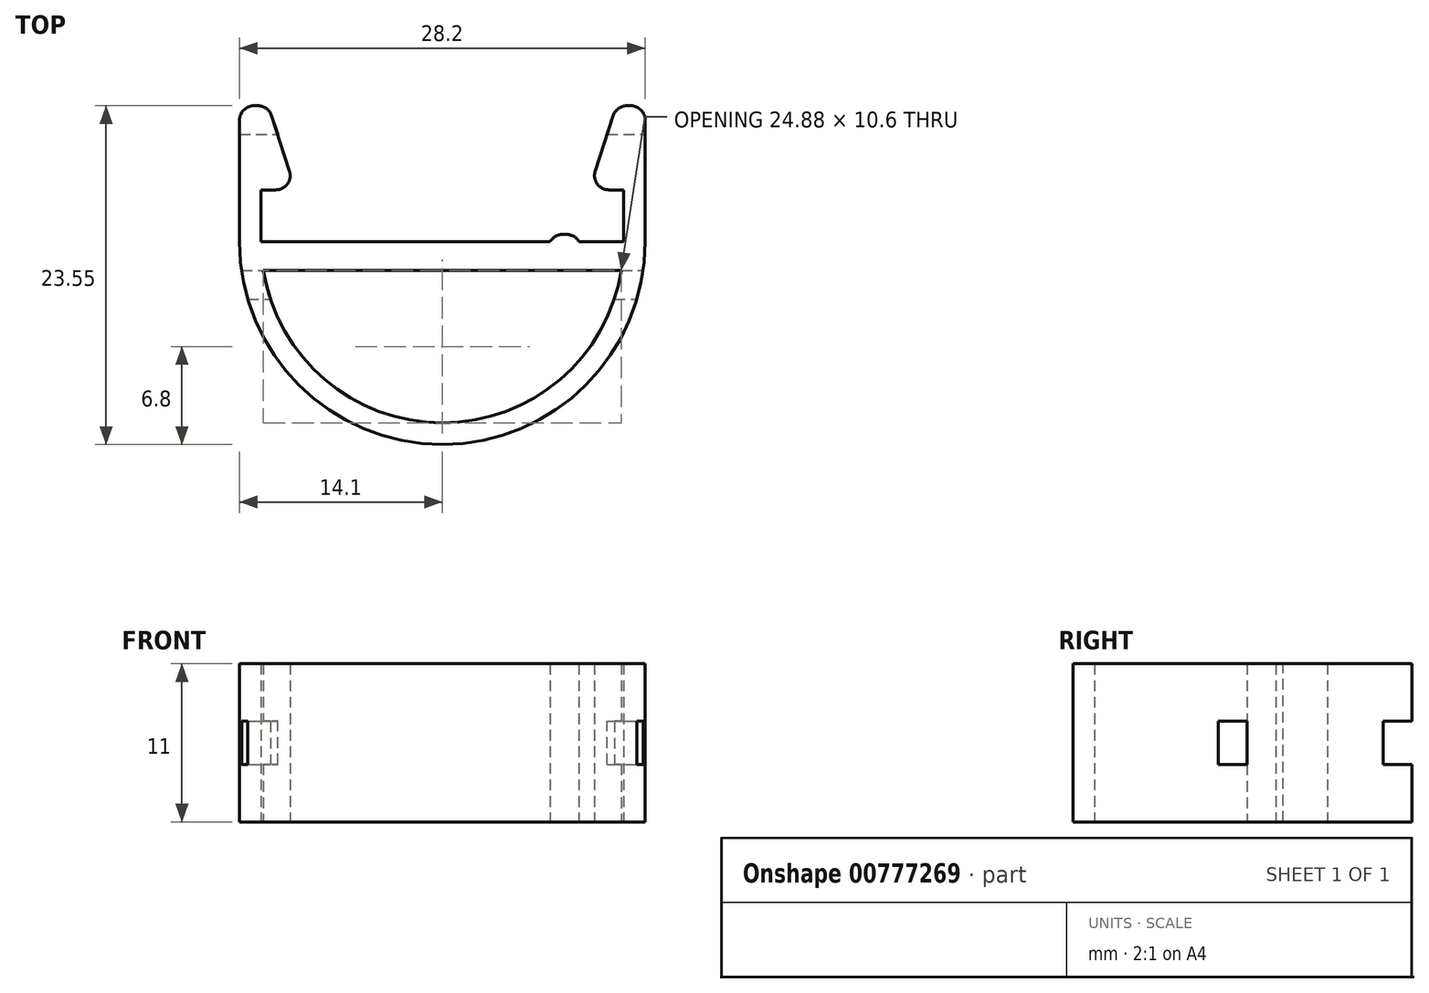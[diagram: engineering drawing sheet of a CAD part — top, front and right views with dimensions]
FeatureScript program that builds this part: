
annotation { "Feature Type Name" : "Feature", "Feature Type Description" : "" }
export const myFeature = defineFeature(function(context is Context, id is Id, definition is map)
    precondition{}
    {
        {
            var Q0;
            Q0=qCreatedBy(makeId("Top.planeOp"),FACE);
            var sketch = newSketch(context, id + "F0", { "sketchPlane" : qUnion([Q0])});
            skArc(sketch, "E0", {"start": v(-14.1, 0) * mm, "mid": v(0, -14.1) * mm, "end": v(14.1, 0) * mm});
            skLineSegment(sketch, "E1", {"start": v(-14.1, 0) * mm, "end": v(-14.1, 9.45) * mm});
            skLineSegment(sketch, "E2", {"start": v(-14.1, 9.45) * mm, "end": v(-12.1, 9.45) * mm});
            skLineSegment(sketch, "E3", {"start": v(-12.1, 9.45) * mm, "end": v(-10.2, 3.6) * mm});
            skLineSegment(sketch, "E4", {"start": v(-10.2, 3.6) * mm, "end": v(-12.6, 3.6) * mm});
            skLineSegment(sketch, "E5", {"start": v(-12.6, 3.6) * mm, "end": v(-12.6, 0) * mm});
            skLineSegment(sketch, "E6", {"start": v(-12.6, 0) * mm, "end": v(0, 0) * mm});
            skLineSegment(sketch, "E7.MirrorCS", {"start": v(12.6, 0) * mm, "end": v(0, 0) * mm});
            skLineSegment(sketch, "E8.MirrorCS", {"start": v(12.6, 3.6) * mm, "end": v(12.6, 0) * mm});
            skLineSegment(sketch, "E9.MirrorCS", {"start": v(10.2, 3.6) * mm, "end": v(12.6, 3.6) * mm});
            skLineSegment(sketch, "E10.MirrorCS", {"start": v(12.1, 9.45) * mm, "end": v(10.2, 3.6) * mm});
            skLineSegment(sketch, "E11.MirrorCS", {"start": v(14.1, 9.45) * mm, "end": v(12.1, 9.45) * mm});
            skLineSegment(sketch, "E12.MirrorCS", {"start": v(14.1, 0) * mm, "end": v(14.1, 9.45) * mm});
            skArc(sketch, "E13", {"start": v(-12.44, -2) * mm, "mid": v(0, -12.6) * mm, "end": v(12.44, -2) * mm});
            skLineSegment(sketch, "E14", {"start": v(-12.44, -2) * mm, "end": v(12.44, -2) * mm});
            skLineSegment(sketch, "E15.bottom", {"start": v(-9.5, 0) * mm, "end": v(-7.5, 0) * mm});
            skLineSegment(sketch, "E15.top", {"start": v(-9.5, 0.5) * mm, "end": v(-7.5, 0.5) * mm});
            skLineSegment(sketch, "E15.left", {"start": v(-9.5, 0) * mm, "end": v(-9.5, 0.5) * mm});
            skLineSegment(sketch, "E15.right", {"start": v(-7.5, 0) * mm, "end": v(-7.5, 0.5) * mm});
            skLineSegment(sketch, "E16.MirrorCS", {"start": v(9.5, 0) * mm, "end": v(9.5, 0.5) * mm});
            skLineSegment(sketch, "E17.MirrorCS", {"start": v(9.5, 0.5) * mm, "end": v(7.5, 0.5) * mm});
            skLineSegment(sketch, "E18.MirrorCS", {"start": v(7.5, 0) * mm, "end": v(7.5, 0.5) * mm});
            skSolve(sketch);
        }
        {
            var Q0;
            Q0=makeQuery(id+"F0.imprint","IMPRINT",FACE,{"disambiguationData":[TD([[makeQuery(id+"F0.imprint","IMPRINT",EDGE,{"derivedFrom":sQuery(id+"F0.wireOp",EDGE,"E0")}),1.0]])]});
            var Q1;
            Q1=makeQuery(id+"F0.imprint","IMPRINT",FACE,{"disambiguationData":[TD([[makeQuery(id+"F0.imprint","IMPRINT",EDGE,{"derivedFrom":sQuery(id+"F0.wireOp",EDGE,"E15.bottom")}),1.0]])]});
            var Q2;
            {var subQ0=sQuery(id+"F0.wireOp",EDGE,"E16.MirrorCS");Q2=makeQuery(id+"F0.imprint","IMPRINT",FACE,{"disambiguationData":[TD([[makeQuery(id+"F0.imprint","IMPRINT",EDGE,{"derivedFrom":subQ0}),1.0]])]});}
            extrude(context, id + "F1", {"entities" : qUnion([Q0, Q1, Q2]), "depth" : 11 * mm, "offsetDistance" : 25 * mm});
        }
        {
            var Q0;
            Q0=makeQuery(id+"F1.opExtrude","SWEPT_EDGE",EDGE,{"disambiguationData":[OSD([sQuery(id+"F0.wireOp",EDGE,"E3"),sQuery(id+"F0.wireOp",EDGE,"E4")])]});
            var Q1;
            Q1=makeQuery(id+"F1.opExtrude","SWEPT_EDGE",EDGE,{"disambiguationData":[OSD([sQuery(id+"F0.wireOp",EDGE,"E1"),sQuery(id+"F0.wireOp",EDGE,"E2")])]});
            var Q2;
            Q2=makeQuery(id+"F1.opExtrude","SWEPT_EDGE",EDGE,{"disambiguationData":[OSD([sQuery(id+"F0.wireOp",EDGE,"E2"),sQuery(id+"F0.wireOp",EDGE,"E3")])]});
            var Q3;
            Q3=makeQuery(id+"F1.opExtrude","SWEPT_EDGE",EDGE,{"disambiguationData":[OSD([sQuery(id+"F0.wireOp",EDGE,"E15.top"),sQuery(id+"F0.wireOp",EDGE,"E15.left")])]});
            var Q4;
            Q4=makeQuery(id+"F1.opExtrude","SWEPT_EDGE",EDGE,{"disambiguationData":[OSD([sQuery(id+"F0.wireOp",EDGE,"E15.top"),sQuery(id+"F0.wireOp",EDGE,"E15.right")])]});
            var Q5;
            Q5=makeQuery(id+"F1.opExtrude","SWEPT_EDGE",EDGE,{"disambiguationData":[OSD([sQuery(id+"F0.wireOp",EDGE,"E17.MirrorCS"),sQuery(id+"F0.wireOp",EDGE,"E18.MirrorCS")])]});
            var Q6;
            Q6=makeQuery(id+"F1.opExtrude","SWEPT_EDGE",EDGE,{"disambiguationData":[OSD([sQuery(id+"F0.wireOp",EDGE,"E16.MirrorCS"),sQuery(id+"F0.wireOp",EDGE,"E17.MirrorCS")])]});
            var Q7;
            Q7=makeQuery(id+"F1.opExtrude","SWEPT_EDGE",EDGE,{"disambiguationData":[OSD([sQuery(id+"F0.wireOp",EDGE,"E9.MirrorCS"),sQuery(id+"F0.wireOp",EDGE,"E10.MirrorCS")])]});
            var Q8;
            Q8=makeQuery(id+"F1.opExtrude","SWEPT_EDGE",EDGE,{"disambiguationData":[OSD([sQuery(id+"F0.wireOp",EDGE,"E10.MirrorCS"),sQuery(id+"F0.wireOp",EDGE,"E11.MirrorCS")])]});
            var Q9;
            Q9=makeQuery(id+"F1.opExtrude","SWEPT_EDGE",EDGE,{"disambiguationData":[OSD([sQuery(id+"F0.wireOp",EDGE,"E11.MirrorCS"),sQuery(id+"F0.wireOp",EDGE,"E12.MirrorCS")])]});
            fillet(context, id + "F2", {"entities" : qUnion([Q0, Q1, Q2, Q3, Q4, Q5, Q6, Q7, Q8, Q9]), "radius" : 1 * mm, "tangentPropagation" : true, "allowEdgeOverflow" : false});
        }
        {
            var Q0;
            Q0=qCreatedBy(makeId("Right.planeOp"),FACE);
            var sketch = newSketch(context, id + "F3", { "sketchPlane" : qUnion([Q0])});
            skLineSegment(sketch, "E19.bottom", {"start": v(-4, 4) * mm, "end": v(-2, 4) * mm});
            skLineSegment(sketch, "E19.top", {"start": v(-4, 7) * mm, "end": v(-2, 7) * mm});
            skLineSegment(sketch, "E19.left", {"start": v(-4, 4) * mm, "end": v(-4, 7) * mm});
            skLineSegment(sketch, "E19.right", {"start": v(-2, 4) * mm, "end": v(-2, 7) * mm});
            skPoint(sketch, "E19.middle", {"position": v(-3, 5.5) * mm});
            skLineSegment(sketch, "E20.bottom", {"start": v(7.45, 4) * mm, "end": v(9.45, 4) * mm});
            skLineSegment(sketch, "E20.top", {"start": v(7.45, 7) * mm, "end": v(9.45, 7) * mm});
            skLineSegment(sketch, "E20.left", {"start": v(7.45, 4) * mm, "end": v(7.45, 7) * mm});
            skLineSegment(sketch, "E20.right", {"start": v(9.45, 4) * mm, "end": v(9.45, 7) * mm});
            skPoint(sketch, "E20.middle", {"position": v(8.45, 5.5) * mm});
            skSolve(sketch);
        }
        {
            var Q0;
            Q0 = qSketchRegion(id + "F3", true);
            extrude(context, id + "F4", {"entities" : qUnion([Q0]), "operationType" : NewBodyOperationType.REMOVE, "endBound" : BoundingType.SYMMETRIC, "oppositeDirection" : true, "depth" : 30 * mm, "offsetDistance" : 25 * mm});
        }
    });
